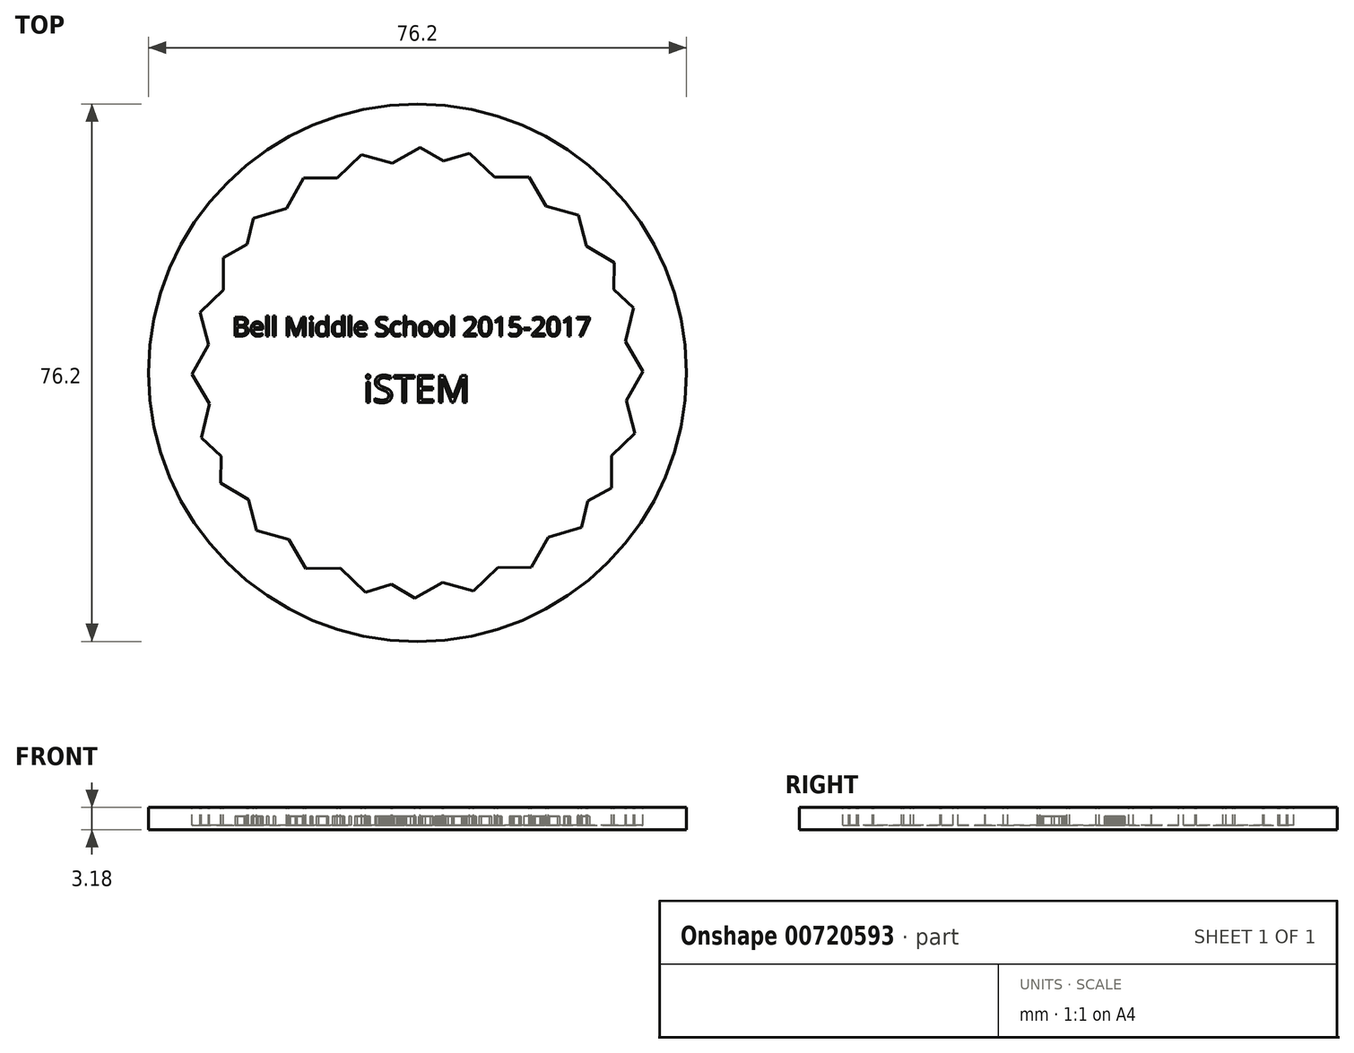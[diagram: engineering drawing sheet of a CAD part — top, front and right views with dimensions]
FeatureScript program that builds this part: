
annotation { "Feature Type Name" : "Feature", "Feature Type Description" : "" }
export const myFeature = defineFeature(function(context is Context, id is Id, definition is map)
    precondition{}
    {
        {
            var Q0;
            Q0=qCreatedBy(makeId("Top.planeOp"),FACE);
            var sketch = newSketch(context, id + "F0", { "sketchPlane" : qUnion([Q0])});
            skCircle(sketch, "E0", {"center": v(0, 0) * mm, "radius": 38.1 * mm});
            skSolve(sketch);
        }
        {
            var Q0;
            Q0=makeQuery(id+"F0.imprint","IMPRINT",FACE,{"disambiguationData":[TD([[makeQuery(id+"F0.imprint","IMPRINT",EDGE,{"derivedFrom":sQuery(id+"F0.wireOp",EDGE,"E0")}),1.0]])]});
            extrude(context, id + "F1", {"entities" : qUnion([Q0]), "depth" : 3.17 * mm, "offsetDistance" : 25.4 * mm});
        }
        {
            var Q0;
            Q0=makeQuery(id+"F1.opExtrude","CAP_FACE",FACE,{"disambiguationData":[OSD([sQuery(id+"F0.wireOp",EDGE,"E0")])],"isStart":false});
            var sketch = newSketch(context, id + "F2", { "sketchPlane" : qUnion([Q0])});
            skCircle(sketch, "E1", {"center": v(0, 0) * mm, "radius": 34.93 * mm});
            skCircle(sketch, "E2.cCircle", {"center": v(0, 0) * mm, "radius": 27.67 * mm, "construction": true});
            skLineSegment(sketch, "E2.0", {"start": v(15.83, 27.75) * mm, "end": v(31.95, 0.17) * mm});
            skLineSegment(sketch, "E2.1", {"start": v(31.95, 0.17) * mm, "end": v(16.12, -27.58) * mm});
            skLineSegment(sketch, "E2.2", {"start": v(16.12, -27.58) * mm, "end": v(-15.83, -27.75) * mm});
            skLineSegment(sketch, "E2.3", {"start": v(-15.83, -27.75) * mm, "end": v(-31.95, -0.17) * mm});
            skLineSegment(sketch, "E2.4", {"start": v(-31.95, -0.17) * mm, "end": v(-16.12, 27.58) * mm});
            skLineSegment(sketch, "E2.5", {"start": v(-16.12, 27.58) * mm, "end": v(15.83, 27.75) * mm});
            skPoint(sketch, "E2.0.midPoint", {"position": v(23.89, 13.96) * mm});
            skLineSegment(sketch, "E3.0", {"start": v(0.4, 31.95) * mm, "end": v(27.87, 15.63) * mm});
            skLineSegment(sketch, "E3.1", {"start": v(27.87, 15.63) * mm, "end": v(27.47, -16.32) * mm});
            skLineSegment(sketch, "E3.2", {"start": v(27.47, -16.32) * mm, "end": v(-0.4, -31.95) * mm});
            skLineSegment(sketch, "E3.3", {"start": v(-0.4, -31.95) * mm, "end": v(-27.87, -15.63) * mm});
            skLineSegment(sketch, "E3.4", {"start": v(-27.87, -15.63) * mm, "end": v(-27.47, 16.32) * mm});
            skLineSegment(sketch, "E3.5", {"start": v(-27.47, 16.32) * mm, "end": v(0.4, 31.95) * mm});
            skPoint(sketch, "E3.0.midPoint", {"position": v(14.13, 23.79) * mm});
            skLineSegment(sketch, "E4.0", {"start": v(22.82, 22.36) * mm, "end": v(30.78, -8.58) * mm});
            skLineSegment(sketch, "E4.1", {"start": v(30.78, -8.58) * mm, "end": v(7.96, -30.94) * mm});
            skLineSegment(sketch, "E4.2", {"start": v(7.96, -30.94) * mm, "end": v(-22.82, -22.36) * mm});
            skLineSegment(sketch, "E4.3", {"start": v(-22.82, -22.36) * mm, "end": v(-30.78, 8.58) * mm});
            skLineSegment(sketch, "E4.4", {"start": v(-30.78, 8.58) * mm, "end": v(-7.96, 30.94) * mm});
            skLineSegment(sketch, "E4.5", {"start": v(-7.96, 30.94) * mm, "end": v(22.82, 22.36) * mm});
            skPoint(sketch, "E4.0.midPoint", {"position": v(26.8, 6.9) * mm});
            skLineSegment(sketch, "E5.0", {"start": v(-23.26, 21.9) * mm, "end": v(7.34, 31.1) * mm});
            skLineSegment(sketch, "E5.1", {"start": v(7.34, 31.1) * mm, "end": v(30.6, 9.19) * mm});
            skLineSegment(sketch, "E5.2", {"start": v(30.6, 9.19) * mm, "end": v(23.26, -21.9) * mm});
            skLineSegment(sketch, "E5.3", {"start": v(23.26, -21.9) * mm, "end": v(-7.34, -31.1) * mm});
            skLineSegment(sketch, "E5.4", {"start": v(-7.34, -31.1) * mm, "end": v(-30.6, -9.19) * mm});
            skLineSegment(sketch, "E5.5", {"start": v(-30.6, -9.19) * mm, "end": v(-23.26, 21.9) * mm});
            skPoint(sketch, "E5.0.midPoint", {"position": v(-7.96, 26.5) * mm});
            skSolve(sketch);
        }
        {
            var Q0;
            {var subQ0=sQuery(id+"F2.wireOp",EDGE,"E4.2");var subQ1=sQuery(id+"F2.wireOp",EDGE,"E2.3");var subQ2=makeQuery(id+"F2.imprint","INTERSECT",VERTEX,{"derivedFrom":[subQ1,subQ0]});Q0=makeQuery(id+"F2.imprint","IMPRINT",FACE,{"disambiguationData":[TD([[makeQuery(id+"F2.imprint","IMPRINT",EDGE,{"disambiguationData":[TD([[subQ2,-1.0]])],"derivedFrom":subQ1}),-1.0]])]});}
            var Q1;
            {var subQ0=sQuery(id+"F2.wireOp",EDGE,"E2.3");var subQ1=sQuery(id+"F2.wireOp",EDGE,"E2.2");var subQ2=makeQuery(id+"F2.imprint","INTERSECT",VERTEX,{"derivedFrom":[subQ1,subQ0]});Q1=makeQuery(id+"F2.imprint","IMPRINT",FACE,{"disambiguationData":[TD([[makeQuery(id+"F2.imprint","IMPRINT",EDGE,{"disambiguationData":[TD([[subQ2,1.0]])],"derivedFrom":subQ1}),-1.0]])]});}
            var Q2;
            {var subQ0=sQuery(id+"F2.wireOp",EDGE,"E4.2");var subQ1=sQuery(id+"F2.wireOp",EDGE,"E2.2");var subQ2=makeQuery(id+"F2.imprint","INTERSECT",VERTEX,{"derivedFrom":[subQ1,subQ0]});Q2=makeQuery(id+"F2.imprint","IMPRINT",FACE,{"disambiguationData":[TD([[makeQuery(id+"F2.imprint","IMPRINT",EDGE,{"disambiguationData":[TD([[subQ2,-1.0]])],"derivedFrom":subQ1}),-1.0]])]});}
            var Q3;
            {var subQ0=sQuery(id+"F2.wireOp",EDGE,"E4.2");var subQ1=sQuery(id+"F2.wireOp",EDGE,"E2.2");var subQ2=makeQuery(id+"F2.imprint","INTERSECT",VERTEX,{"derivedFrom":[subQ1,subQ0]});Q3=makeQuery(id+"F2.imprint","IMPRINT",FACE,{"disambiguationData":[TD([[makeQuery(id+"F2.imprint","IMPRINT",EDGE,{"disambiguationData":[TD([[subQ2,-1.0]])],"derivedFrom":subQ1}),1.0]])]});}
            var Q4;
            {var subQ0=sQuery(id+"F2.wireOp",EDGE,"E3.2");var subQ1=sQuery(id+"F2.wireOp",EDGE,"E2.2");var subQ2=makeQuery(id+"F2.imprint","INTERSECT",VERTEX,{"derivedFrom":[subQ1,subQ0]});Q4=makeQuery(id+"F2.imprint","IMPRINT",FACE,{"disambiguationData":[TD([[makeQuery(id+"F2.imprint","IMPRINT",EDGE,{"disambiguationData":[TD([[subQ2,-1.0]])],"derivedFrom":subQ1}),1.0]])]});}
            var Q5;
            {var subQ0=sQuery(id+"F2.wireOp",EDGE,"E4.1");var subQ1=sQuery(id+"F2.wireOp",EDGE,"E2.2");var subQ2=makeQuery(id+"F2.imprint","INTERSECT",VERTEX,{"derivedFrom":[subQ1,subQ0]});Q5=makeQuery(id+"F2.imprint","IMPRINT",FACE,{"disambiguationData":[TD([[makeQuery(id+"F2.imprint","IMPRINT",EDGE,{"disambiguationData":[TD([[subQ2,-1.0]])],"derivedFrom":subQ1}),1.0]])]});}
            var Q6;
            {var subQ0=sQuery(id+"F2.wireOp",EDGE,"E4.1");var subQ1=sQuery(id+"F2.wireOp",EDGE,"E2.2");var subQ2=makeQuery(id+"F2.imprint","INTERSECT",VERTEX,{"derivedFrom":[subQ1,subQ0]});Q6=makeQuery(id+"F2.imprint","IMPRINT",FACE,{"disambiguationData":[TD([[makeQuery(id+"F2.imprint","IMPRINT",EDGE,{"disambiguationData":[TD([[subQ2,-1.0]])],"derivedFrom":subQ1}),-1.0]])]});}
            var Q7;
            {var subQ0=sQuery(id+"F2.wireOp",EDGE,"E2.2");var subQ1=sQuery(id+"F2.wireOp",EDGE,"E2.1");var subQ2=makeQuery(id+"F2.imprint","INTERSECT",VERTEX,{"derivedFrom":[subQ1,subQ0]});Q7=makeQuery(id+"F2.imprint","IMPRINT",FACE,{"disambiguationData":[TD([[makeQuery(id+"F2.imprint","IMPRINT",EDGE,{"disambiguationData":[TD([[subQ2,1.0]])],"derivedFrom":subQ1}),-1.0]])]});}
            var Q8;
            {var subQ15=sQuery(id+"F2.wireOp",EDGE,"E3.0");var subQ16=sQuery(id+"F2.wireOp",EDGE,"E2.0");var subQ17=makeQuery(id+"F2.imprint","INTERSECT",VERTEX,{"derivedFrom":[subQ16,subQ15]});Q8=makeQuery(id+"F2.imprint","IMPRINT",FACE,{"disambiguationData":[TD([[makeQuery(id+"F2.imprint","IMPRINT",EDGE,{"disambiguationData":[TD([[subQ17,-1.0]])],"derivedFrom":subQ16}),-1.0]])]});}
            var Q9;
            {var subQ0=sQuery(id+"F2.wireOp",EDGE,"E4.1");var subQ1=sQuery(id+"F2.wireOp",EDGE,"E2.1");var subQ2=makeQuery(id+"F2.imprint","INTERSECT",VERTEX,{"derivedFrom":[subQ1,subQ0]});Q9=makeQuery(id+"F2.imprint","IMPRINT",FACE,{"disambiguationData":[TD([[makeQuery(id+"F2.imprint","IMPRINT",EDGE,{"disambiguationData":[TD([[subQ2,-1.0]])],"derivedFrom":subQ1}),-1.0]])]});}
            var Q10;
            {var subQ0=sQuery(id+"F2.wireOp",EDGE,"E4.1");var subQ1=sQuery(id+"F2.wireOp",EDGE,"E2.1");var subQ2=makeQuery(id+"F2.imprint","INTERSECT",VERTEX,{"derivedFrom":[subQ1,subQ0]});Q10=makeQuery(id+"F2.imprint","IMPRINT",FACE,{"disambiguationData":[TD([[makeQuery(id+"F2.imprint","IMPRINT",EDGE,{"disambiguationData":[TD([[subQ2,-1.0]])],"derivedFrom":subQ1}),1.0]])]});}
            var Q11;
            {var subQ0=sQuery(id+"F2.wireOp",EDGE,"E3.1");var subQ1=sQuery(id+"F2.wireOp",EDGE,"E2.1");var subQ2=makeQuery(id+"F2.imprint","INTERSECT",VERTEX,{"derivedFrom":[subQ1,subQ0]});Q11=makeQuery(id+"F2.imprint","IMPRINT",FACE,{"disambiguationData":[TD([[makeQuery(id+"F2.imprint","IMPRINT",EDGE,{"disambiguationData":[TD([[subQ2,-1.0]])],"derivedFrom":subQ1}),1.0]])]});}
            var Q12;
            {var subQ0=sQuery(id+"F2.wireOp",EDGE,"E4.0");var subQ1=sQuery(id+"F2.wireOp",EDGE,"E2.1");var subQ2=makeQuery(id+"F2.imprint","INTERSECT",VERTEX,{"derivedFrom":[subQ1,subQ0]});Q12=makeQuery(id+"F2.imprint","IMPRINT",FACE,{"disambiguationData":[TD([[makeQuery(id+"F2.imprint","IMPRINT",EDGE,{"disambiguationData":[TD([[subQ2,-1.0]])],"derivedFrom":subQ1}),1.0]])]});}
            var Q13;
            {var subQ0=sQuery(id+"F2.wireOp",EDGE,"E4.0");var subQ1=sQuery(id+"F2.wireOp",EDGE,"E2.1");var subQ2=makeQuery(id+"F2.imprint","INTERSECT",VERTEX,{"derivedFrom":[subQ1,subQ0]});Q13=makeQuery(id+"F2.imprint","IMPRINT",FACE,{"disambiguationData":[TD([[makeQuery(id+"F2.imprint","IMPRINT",EDGE,{"disambiguationData":[TD([[subQ2,-1.0]])],"derivedFrom":subQ1}),-1.0]])]});}
            var Q14;
            {var subQ0=sQuery(id+"F2.wireOp",EDGE,"E2.1");var subQ1=sQuery(id+"F2.wireOp",EDGE,"E2.0");var subQ2=makeQuery(id+"F2.imprint","INTERSECT",VERTEX,{"derivedFrom":[subQ1,subQ0]});Q14=makeQuery(id+"F2.imprint","IMPRINT",FACE,{"disambiguationData":[TD([[makeQuery(id+"F2.imprint","IMPRINT",EDGE,{"disambiguationData":[TD([[subQ2,1.0]])],"derivedFrom":subQ1}),-1.0]])]});}
            var Q15;
            {var subQ0=sQuery(id+"F2.wireOp",EDGE,"E4.0");var subQ1=sQuery(id+"F2.wireOp",EDGE,"E2.0");var subQ2=makeQuery(id+"F2.imprint","INTERSECT",VERTEX,{"derivedFrom":[subQ1,subQ0]});Q15=makeQuery(id+"F2.imprint","IMPRINT",FACE,{"disambiguationData":[TD([[makeQuery(id+"F2.imprint","IMPRINT",EDGE,{"disambiguationData":[TD([[subQ2,-1.0]])],"derivedFrom":subQ1}),-1.0]])]});}
            var Q16;
            {var subQ0=sQuery(id+"F2.wireOp",EDGE,"E4.0");var subQ1=sQuery(id+"F2.wireOp",EDGE,"E2.0");var subQ2=makeQuery(id+"F2.imprint","INTERSECT",VERTEX,{"derivedFrom":[subQ1,subQ0]});Q16=makeQuery(id+"F2.imprint","IMPRINT",FACE,{"disambiguationData":[TD([[makeQuery(id+"F2.imprint","IMPRINT",EDGE,{"disambiguationData":[TD([[subQ2,-1.0]])],"derivedFrom":subQ1}),1.0]])]});}
            var Q17;
            {var subQ0=sQuery(id+"F2.wireOp",EDGE,"E3.0");var subQ1=sQuery(id+"F2.wireOp",EDGE,"E2.0");var subQ2=makeQuery(id+"F2.imprint","INTERSECT",VERTEX,{"derivedFrom":[subQ1,subQ0]});Q17=makeQuery(id+"F2.imprint","IMPRINT",FACE,{"disambiguationData":[TD([[makeQuery(id+"F2.imprint","IMPRINT",EDGE,{"disambiguationData":[TD([[subQ2,-1.0]])],"derivedFrom":subQ1}),1.0]])]});}
            var Q18;
            {var subQ0=sQuery(id+"F2.wireOp",EDGE,"E4.5");var subQ1=sQuery(id+"F2.wireOp",EDGE,"E2.0");var subQ2=makeQuery(id+"F2.imprint","INTERSECT",VERTEX,{"derivedFrom":[subQ1,subQ0]});Q18=makeQuery(id+"F2.imprint","IMPRINT",FACE,{"disambiguationData":[TD([[makeQuery(id+"F2.imprint","IMPRINT",EDGE,{"disambiguationData":[TD([[subQ2,-1.0]])],"derivedFrom":subQ1}),1.0]])]});}
            var Q19;
            {var subQ0=sQuery(id+"F2.wireOp",EDGE,"E4.5");var subQ1=sQuery(id+"F2.wireOp",EDGE,"E2.0");var subQ2=makeQuery(id+"F2.imprint","INTERSECT",VERTEX,{"derivedFrom":[subQ1,subQ0]});Q19=makeQuery(id+"F2.imprint","IMPRINT",FACE,{"disambiguationData":[TD([[makeQuery(id+"F2.imprint","IMPRINT",EDGE,{"disambiguationData":[TD([[subQ2,-1.0]])],"derivedFrom":subQ1}),-1.0]])]});}
            var Q20;
            {var subQ0=sQuery(id+"F2.wireOp",EDGE,"E2.5");var subQ1=sQuery(id+"F2.wireOp",EDGE,"E2.0");var subQ2=makeQuery(id+"F2.imprint","INTERSECT",VERTEX,{"derivedFrom":[subQ1,subQ0]});Q20=makeQuery(id+"F2.imprint","IMPRINT",FACE,{"disambiguationData":[TD([[makeQuery(id+"F2.imprint","IMPRINT",EDGE,{"disambiguationData":[TD([[subQ2,-1.0]])],"derivedFrom":subQ1}),-1.0]])]});}
            var Q21;
            {var subQ0=sQuery(id+"F2.wireOp",EDGE,"E4.5");var subQ1=sQuery(id+"F2.wireOp",EDGE,"E2.5");var subQ2=makeQuery(id+"F2.imprint","INTERSECT",VERTEX,{"derivedFrom":[subQ1,subQ0]});Q21=makeQuery(id+"F2.imprint","IMPRINT",FACE,{"disambiguationData":[TD([[makeQuery(id+"F2.imprint","IMPRINT",EDGE,{"disambiguationData":[TD([[subQ2,-1.0]])],"derivedFrom":subQ1}),1.0]])]});}
            var Q22;
            {var subQ0=sQuery(id+"F2.wireOp",EDGE,"E3.5");var subQ1=sQuery(id+"F2.wireOp",EDGE,"E2.5");var subQ2=makeQuery(id+"F2.imprint","INTERSECT",VERTEX,{"derivedFrom":[subQ1,subQ0]});Q22=makeQuery(id+"F2.imprint","IMPRINT",FACE,{"disambiguationData":[TD([[makeQuery(id+"F2.imprint","IMPRINT",EDGE,{"disambiguationData":[TD([[subQ2,-1.0]])],"derivedFrom":subQ1}),1.0]])]});}
            var Q23;
            {var subQ0=sQuery(id+"F2.wireOp",EDGE,"E4.5");var subQ1=sQuery(id+"F2.wireOp",EDGE,"E2.5");var subQ2=makeQuery(id+"F2.imprint","INTERSECT",VERTEX,{"derivedFrom":[subQ1,subQ0]});Q23=makeQuery(id+"F2.imprint","IMPRINT",FACE,{"disambiguationData":[TD([[makeQuery(id+"F2.imprint","IMPRINT",EDGE,{"disambiguationData":[TD([[subQ2,-1.0]])],"derivedFrom":subQ1}),-1.0]])]});}
            var Q24;
            {var subQ0=sQuery(id+"F2.wireOp",EDGE,"E4.4");var subQ1=sQuery(id+"F2.wireOp",EDGE,"E2.5");var subQ2=makeQuery(id+"F2.imprint","INTERSECT",VERTEX,{"derivedFrom":[subQ1,subQ0]});Q24=makeQuery(id+"F2.imprint","IMPRINT",FACE,{"disambiguationData":[TD([[makeQuery(id+"F2.imprint","IMPRINT",EDGE,{"disambiguationData":[TD([[subQ2,-1.0]])],"derivedFrom":subQ1}),-1.0]])]});}
            var Q25;
            {var subQ0=sQuery(id+"F2.wireOp",EDGE,"E4.4");var subQ1=sQuery(id+"F2.wireOp",EDGE,"E2.5");var subQ2=makeQuery(id+"F2.imprint","INTERSECT",VERTEX,{"derivedFrom":[subQ1,subQ0]});Q25=makeQuery(id+"F2.imprint","IMPRINT",FACE,{"disambiguationData":[TD([[makeQuery(id+"F2.imprint","IMPRINT",EDGE,{"disambiguationData":[TD([[subQ2,-1.0]])],"derivedFrom":subQ1}),1.0]])]});}
            var Q26;
            {var subQ0=sQuery(id+"F2.wireOp",EDGE,"E2.5");var subQ1=sQuery(id+"F2.wireOp",EDGE,"E2.4");var subQ2=makeQuery(id+"F2.imprint","INTERSECT",VERTEX,{"derivedFrom":[subQ1,subQ0]});Q26=makeQuery(id+"F2.imprint","IMPRINT",FACE,{"disambiguationData":[TD([[makeQuery(id+"F2.imprint","IMPRINT",EDGE,{"disambiguationData":[TD([[subQ2,1.0]])],"derivedFrom":subQ1}),-1.0]])]});}
            var Q27;
            {var subQ0=sQuery(id+"F2.wireOp",EDGE,"E4.4");var subQ1=sQuery(id+"F2.wireOp",EDGE,"E2.4");var subQ2=makeQuery(id+"F2.imprint","INTERSECT",VERTEX,{"derivedFrom":[subQ1,subQ0]});Q27=makeQuery(id+"F2.imprint","IMPRINT",FACE,{"disambiguationData":[TD([[makeQuery(id+"F2.imprint","IMPRINT",EDGE,{"disambiguationData":[TD([[subQ2,-1.0]])],"derivedFrom":subQ1}),-1.0]])]});}
            var Q28;
            {var subQ0=sQuery(id+"F2.wireOp",EDGE,"E4.4");var subQ1=sQuery(id+"F2.wireOp",EDGE,"E2.4");var subQ2=makeQuery(id+"F2.imprint","INTERSECT",VERTEX,{"derivedFrom":[subQ1,subQ0]});Q28=makeQuery(id+"F2.imprint","IMPRINT",FACE,{"disambiguationData":[TD([[makeQuery(id+"F2.imprint","IMPRINT",EDGE,{"disambiguationData":[TD([[subQ2,-1.0]])],"derivedFrom":subQ1}),1.0]])]});}
            var Q29;
            {var subQ0=sQuery(id+"F2.wireOp",EDGE,"E3.4");var subQ1=sQuery(id+"F2.wireOp",EDGE,"E2.4");var subQ2=makeQuery(id+"F2.imprint","INTERSECT",VERTEX,{"derivedFrom":[subQ1,subQ0]});Q29=makeQuery(id+"F2.imprint","IMPRINT",FACE,{"disambiguationData":[TD([[makeQuery(id+"F2.imprint","IMPRINT",EDGE,{"disambiguationData":[TD([[subQ2,-1.0]])],"derivedFrom":subQ1}),1.0]])]});}
            var Q30;
            {var subQ0=sQuery(id+"F2.wireOp",EDGE,"E4.3");var subQ1=sQuery(id+"F2.wireOp",EDGE,"E2.4");var subQ2=makeQuery(id+"F2.imprint","INTERSECT",VERTEX,{"derivedFrom":[subQ1,subQ0]});Q30=makeQuery(id+"F2.imprint","IMPRINT",FACE,{"disambiguationData":[TD([[makeQuery(id+"F2.imprint","IMPRINT",EDGE,{"disambiguationData":[TD([[subQ2,-1.0]])],"derivedFrom":subQ1}),1.0]])]});}
            var Q31;
            {var subQ0=sQuery(id+"F2.wireOp",EDGE,"E4.3");var subQ1=sQuery(id+"F2.wireOp",EDGE,"E2.4");var subQ2=makeQuery(id+"F2.imprint","INTERSECT",VERTEX,{"derivedFrom":[subQ1,subQ0]});Q31=makeQuery(id+"F2.imprint","IMPRINT",FACE,{"disambiguationData":[TD([[makeQuery(id+"F2.imprint","IMPRINT",EDGE,{"disambiguationData":[TD([[subQ2,-1.0]])],"derivedFrom":subQ1}),-1.0]])]});}
            var Q32;
            {var subQ0=sQuery(id+"F2.wireOp",EDGE,"E2.4");var subQ1=sQuery(id+"F2.wireOp",EDGE,"E2.3");var subQ2=makeQuery(id+"F2.imprint","INTERSECT",VERTEX,{"derivedFrom":[subQ1,subQ0]});Q32=makeQuery(id+"F2.imprint","IMPRINT",FACE,{"disambiguationData":[TD([[makeQuery(id+"F2.imprint","IMPRINT",EDGE,{"disambiguationData":[TD([[subQ2,1.0]])],"derivedFrom":subQ1}),-1.0]])]});}
            var Q33;
            {var subQ0=sQuery(id+"F2.wireOp",EDGE,"E4.3");var subQ1=sQuery(id+"F2.wireOp",EDGE,"E2.3");var subQ2=makeQuery(id+"F2.imprint","INTERSECT",VERTEX,{"derivedFrom":[subQ1,subQ0]});Q33=makeQuery(id+"F2.imprint","IMPRINT",FACE,{"disambiguationData":[TD([[makeQuery(id+"F2.imprint","IMPRINT",EDGE,{"disambiguationData":[TD([[subQ2,-1.0]])],"derivedFrom":subQ1}),-1.0]])]});}
            var Q34;
            {var subQ0=sQuery(id+"F2.wireOp",EDGE,"E3.3");var subQ1=sQuery(id+"F2.wireOp",EDGE,"E2.3");var subQ2=makeQuery(id+"F2.imprint","INTERSECT",VERTEX,{"derivedFrom":[subQ1,subQ0]});Q34=makeQuery(id+"F2.imprint","IMPRINT",FACE,{"disambiguationData":[TD([[makeQuery(id+"F2.imprint","IMPRINT",EDGE,{"disambiguationData":[TD([[subQ2,-1.0]])],"derivedFrom":subQ1}),1.0]])]});}
            var Q35;
            {var subQ0=sQuery(id+"F2.wireOp",EDGE,"E4.3");var subQ1=sQuery(id+"F2.wireOp",EDGE,"E2.3");var subQ2=makeQuery(id+"F2.imprint","INTERSECT",VERTEX,{"derivedFrom":[subQ1,subQ0]});Q35=makeQuery(id+"F2.imprint","IMPRINT",FACE,{"disambiguationData":[TD([[makeQuery(id+"F2.imprint","IMPRINT",EDGE,{"disambiguationData":[TD([[subQ2,-1.0]])],"derivedFrom":subQ1}),1.0]])]});}
            var Q36;
            {var subQ0=sQuery(id+"F2.wireOp",EDGE,"E3.4");var subQ1=sQuery(id+"F2.wireOp",EDGE,"E3.3");var subQ2=makeQuery(id+"F2.imprint","INTERSECT",VERTEX,{"derivedFrom":[subQ1,subQ0]});Q36=makeQuery(id+"F2.imprint","IMPRINT",FACE,{"disambiguationData":[TD([[makeQuery(id+"F2.imprint","IMPRINT",EDGE,{"disambiguationData":[TD([[subQ2,1.0]])],"derivedFrom":subQ1}),-1.0]])]});}
            var Q37;
            {var subQ0=sQuery(id+"F2.wireOp",EDGE,"E3.4");var subQ1=sQuery(id+"F2.wireOp",EDGE,"E2.3");var subQ2=makeQuery(id+"F2.imprint","INTERSECT",VERTEX,{"derivedFrom":[subQ1,subQ0]});Q37=makeQuery(id+"F2.imprint","IMPRINT",FACE,{"disambiguationData":[TD([[makeQuery(id+"F2.imprint","IMPRINT",EDGE,{"disambiguationData":[TD([[subQ2,-1.0]])],"derivedFrom":subQ1}),1.0]])]});}
            var Q38;
            {var subQ0=sQuery(id+"F2.wireOp",EDGE,"E3.4");var subQ1=sQuery(id+"F2.wireOp",EDGE,"E2.3");var subQ2=makeQuery(id+"F2.imprint","INTERSECT",VERTEX,{"derivedFrom":[subQ1,subQ0]});Q38=makeQuery(id+"F2.imprint","IMPRINT",FACE,{"disambiguationData":[TD([[makeQuery(id+"F2.imprint","IMPRINT",EDGE,{"disambiguationData":[TD([[subQ2,-1.0]])],"derivedFrom":subQ1}),-1.0]])]});}
            var Q39;
            {var subQ0=sQuery(id+"F2.wireOp",EDGE,"E4.3");var subQ1=sQuery(id+"F2.wireOp",EDGE,"E3.4");var subQ2=makeQuery(id+"F2.imprint","INTERSECT",VERTEX,{"derivedFrom":[subQ1,subQ0]});Q39=makeQuery(id+"F2.imprint","IMPRINT",FACE,{"disambiguationData":[TD([[makeQuery(id+"F2.imprint","IMPRINT",EDGE,{"disambiguationData":[TD([[subQ2,-1.0]])],"derivedFrom":subQ1}),1.0]])]});}
            var Q40;
            {var subQ0=sQuery(id+"F2.wireOp",EDGE,"E3.4");var subQ1=sQuery(id+"F2.wireOp",EDGE,"E2.4");var subQ2=makeQuery(id+"F2.imprint","INTERSECT",VERTEX,{"derivedFrom":[subQ1,subQ0]});Q40=makeQuery(id+"F2.imprint","IMPRINT",FACE,{"disambiguationData":[TD([[makeQuery(id+"F2.imprint","IMPRINT",EDGE,{"disambiguationData":[TD([[subQ2,-1.0]])],"derivedFrom":subQ1}),-1.0]])]});}
            var Q41;
            {var subQ0=sQuery(id+"F2.wireOp",EDGE,"E5.5");var subQ1=sQuery(id+"F2.wireOp",EDGE,"E2.4");var subQ2=makeQuery(id+"F2.imprint","INTERSECT",VERTEX,{"derivedFrom":[subQ1,subQ0]});Q41=makeQuery(id+"F2.imprint","IMPRINT",FACE,{"disambiguationData":[TD([[makeQuery(id+"F2.imprint","IMPRINT",EDGE,{"disambiguationData":[TD([[subQ2,-1.0]])],"derivedFrom":subQ1}),1.0]])]});}
            var Q42;
            {var subQ0=sQuery(id+"F2.wireOp",EDGE,"E3.5");var subQ1=sQuery(id+"F2.wireOp",EDGE,"E3.4");var subQ2=makeQuery(id+"F2.imprint","INTERSECT",VERTEX,{"derivedFrom":[subQ1,subQ0]});Q42=makeQuery(id+"F2.imprint","IMPRINT",FACE,{"disambiguationData":[TD([[makeQuery(id+"F2.imprint","IMPRINT",EDGE,{"disambiguationData":[TD([[subQ2,1.0]])],"derivedFrom":subQ1}),-1.0]])]});}
            var Q43;
            {var subQ0=sQuery(id+"F2.wireOp",EDGE,"E3.5");var subQ1=sQuery(id+"F2.wireOp",EDGE,"E2.4");var subQ2=makeQuery(id+"F2.imprint","INTERSECT",VERTEX,{"derivedFrom":[subQ1,subQ0]});Q43=makeQuery(id+"F2.imprint","IMPRINT",FACE,{"disambiguationData":[TD([[makeQuery(id+"F2.imprint","IMPRINT",EDGE,{"disambiguationData":[TD([[subQ2,-1.0]])],"derivedFrom":subQ1}),1.0]])]});}
            var Q44;
            {var subQ0=sQuery(id+"F2.wireOp",EDGE,"E3.0");var subQ1=sQuery(id+"F2.wireOp",EDGE,"E2.5");var subQ2=makeQuery(id+"F2.imprint","INTERSECT",VERTEX,{"derivedFrom":[subQ1,subQ0]});Q44=makeQuery(id+"F2.imprint","IMPRINT",FACE,{"disambiguationData":[TD([[makeQuery(id+"F2.imprint","IMPRINT",EDGE,{"disambiguationData":[TD([[subQ2,-1.0]])],"derivedFrom":subQ1}),1.0]])]});}
            var Q45;
            {var subQ0=sQuery(id+"F2.wireOp",EDGE,"E3.5");var subQ1=sQuery(id+"F2.wireOp",EDGE,"E3.0");var subQ2=makeQuery(id+"F2.imprint","INTERSECT",VERTEX,{"derivedFrom":[subQ1,subQ0]});Q45=makeQuery(id+"F2.imprint","IMPRINT",FACE,{"disambiguationData":[TD([[makeQuery(id+"F2.imprint","IMPRINT",EDGE,{"disambiguationData":[TD([[subQ2,-1.0]])],"derivedFrom":subQ1}),-1.0]])]});}
            var Q46;
            {var subQ0=sQuery(id+"F2.wireOp",EDGE,"E5.0");var subQ1=sQuery(id+"F2.wireOp",EDGE,"E2.5");var subQ2=makeQuery(id+"F2.imprint","INTERSECT",VERTEX,{"derivedFrom":[subQ1,subQ0]});Q46=makeQuery(id+"F2.imprint","IMPRINT",FACE,{"disambiguationData":[TD([[makeQuery(id+"F2.imprint","IMPRINT",EDGE,{"disambiguationData":[TD([[subQ2,-1.0]])],"derivedFrom":subQ1}),1.0]])]});}
            var Q47;
            {var subQ0=sQuery(id+"F2.wireOp",EDGE,"E3.5");var subQ1=sQuery(id+"F2.wireOp",EDGE,"E2.5");var subQ2=makeQuery(id+"F2.imprint","INTERSECT",VERTEX,{"derivedFrom":[subQ1,subQ0]});Q47=makeQuery(id+"F2.imprint","IMPRINT",FACE,{"disambiguationData":[TD([[makeQuery(id+"F2.imprint","IMPRINT",EDGE,{"disambiguationData":[TD([[subQ2,-1.0]])],"derivedFrom":subQ1}),-1.0]])]});}
            var Q48;
            {var subQ0=sQuery(id+"F2.wireOp",EDGE,"E3.5");var subQ1=sQuery(id+"F2.wireOp",EDGE,"E2.4");var subQ2=makeQuery(id+"F2.imprint","INTERSECT",VERTEX,{"derivedFrom":[subQ1,subQ0]});Q48=makeQuery(id+"F2.imprint","IMPRINT",FACE,{"disambiguationData":[TD([[makeQuery(id+"F2.imprint","IMPRINT",EDGE,{"disambiguationData":[TD([[subQ2,-1.0]])],"derivedFrom":subQ1}),-1.0]])]});}
            var Q49;
            {var subQ0=sQuery(id+"F2.wireOp",EDGE,"E3.1");var subQ1=sQuery(id+"F2.wireOp",EDGE,"E2.0");var subQ2=makeQuery(id+"F2.imprint","INTERSECT",VERTEX,{"derivedFrom":[subQ1,subQ0]});Q49=makeQuery(id+"F2.imprint","IMPRINT",FACE,{"disambiguationData":[TD([[makeQuery(id+"F2.imprint","IMPRINT",EDGE,{"disambiguationData":[TD([[subQ2,-1.0]])],"derivedFrom":subQ1}),1.0]])]});}
            var Q50;
            {var subQ0=sQuery(id+"F2.wireOp",EDGE,"E3.1");var subQ1=sQuery(id+"F2.wireOp",EDGE,"E3.0");var subQ2=makeQuery(id+"F2.imprint","INTERSECT",VERTEX,{"derivedFrom":[subQ1,subQ0]});Q50=makeQuery(id+"F2.imprint","IMPRINT",FACE,{"disambiguationData":[TD([[makeQuery(id+"F2.imprint","IMPRINT",EDGE,{"disambiguationData":[TD([[subQ2,1.0]])],"derivedFrom":subQ1}),-1.0]])]});}
            var Q51;
            {var subQ0=sQuery(id+"F2.wireOp",EDGE,"E3.1");var subQ1=sQuery(id+"F2.wireOp",EDGE,"E2.0");var subQ2=makeQuery(id+"F2.imprint","INTERSECT",VERTEX,{"derivedFrom":[subQ1,subQ0]});Q51=makeQuery(id+"F2.imprint","IMPRINT",FACE,{"disambiguationData":[TD([[makeQuery(id+"F2.imprint","IMPRINT",EDGE,{"disambiguationData":[TD([[subQ2,-1.0]])],"derivedFrom":subQ1}),-1.0]])]});}
            var Q52;
            {var subQ0=sQuery(id+"F2.wireOp",EDGE,"E3.2");var subQ1=sQuery(id+"F2.wireOp",EDGE,"E3.1");var subQ2=makeQuery(id+"F2.imprint","INTERSECT",VERTEX,{"derivedFrom":[subQ1,subQ0]});Q52=makeQuery(id+"F2.imprint","IMPRINT",FACE,{"disambiguationData":[TD([[makeQuery(id+"F2.imprint","IMPRINT",EDGE,{"disambiguationData":[TD([[subQ2,1.0]])],"derivedFrom":subQ1}),-1.0]])]});}
            var Q53;
            {var subQ0=sQuery(id+"F2.wireOp",EDGE,"E3.2");var subQ1=sQuery(id+"F2.wireOp",EDGE,"E2.1");var subQ2=makeQuery(id+"F2.imprint","INTERSECT",VERTEX,{"derivedFrom":[subQ1,subQ0]});Q53=makeQuery(id+"F2.imprint","IMPRINT",FACE,{"disambiguationData":[TD([[makeQuery(id+"F2.imprint","IMPRINT",EDGE,{"disambiguationData":[TD([[subQ2,-1.0]])],"derivedFrom":subQ1}),1.0]])]});}
            var Q54;
            {var subQ0=sQuery(id+"F2.wireOp",EDGE,"E3.2");var subQ1=sQuery(id+"F2.wireOp",EDGE,"E2.1");var subQ2=makeQuery(id+"F2.imprint","INTERSECT",VERTEX,{"derivedFrom":[subQ1,subQ0]});Q54=makeQuery(id+"F2.imprint","IMPRINT",FACE,{"disambiguationData":[TD([[makeQuery(id+"F2.imprint","IMPRINT",EDGE,{"disambiguationData":[TD([[subQ2,-1.0]])],"derivedFrom":subQ1}),-1.0]])]});}
            var Q55;
            {var subQ0=sQuery(id+"F2.wireOp",EDGE,"E3.3");var subQ1=sQuery(id+"F2.wireOp",EDGE,"E3.2");var subQ2=makeQuery(id+"F2.imprint","INTERSECT",VERTEX,{"derivedFrom":[subQ1,subQ0]});Q55=makeQuery(id+"F2.imprint","IMPRINT",FACE,{"disambiguationData":[TD([[makeQuery(id+"F2.imprint","IMPRINT",EDGE,{"disambiguationData":[TD([[subQ2,1.0]])],"derivedFrom":subQ1}),-1.0]])]});}
            var Q56;
            {var subQ0=sQuery(id+"F2.wireOp",EDGE,"E3.3");var subQ1=sQuery(id+"F2.wireOp",EDGE,"E2.2");var subQ2=makeQuery(id+"F2.imprint","INTERSECT",VERTEX,{"derivedFrom":[subQ1,subQ0]});Q56=makeQuery(id+"F2.imprint","IMPRINT",FACE,{"disambiguationData":[TD([[makeQuery(id+"F2.imprint","IMPRINT",EDGE,{"disambiguationData":[TD([[subQ2,-1.0]])],"derivedFrom":subQ1}),1.0]])]});}
            var Q57;
            {var subQ0=sQuery(id+"F2.wireOp",EDGE,"E3.3");var subQ1=sQuery(id+"F2.wireOp",EDGE,"E2.2");var subQ2=makeQuery(id+"F2.imprint","INTERSECT",VERTEX,{"derivedFrom":[subQ1,subQ0]});Q57=makeQuery(id+"F2.imprint","IMPRINT",FACE,{"disambiguationData":[TD([[makeQuery(id+"F2.imprint","IMPRINT",EDGE,{"disambiguationData":[TD([[subQ2,-1.0]])],"derivedFrom":subQ1}),-1.0]])]});}
            var Q58;
            {var subQ0=sQuery(id+"F2.wireOp",EDGE,"E3.0");var subQ1=sQuery(id+"F2.wireOp",EDGE,"E2.5");var subQ2=makeQuery(id+"F2.imprint","INTERSECT",VERTEX,{"derivedFrom":[subQ1,subQ0]});Q58=makeQuery(id+"F2.imprint","IMPRINT",FACE,{"disambiguationData":[TD([[makeQuery(id+"F2.imprint","IMPRINT",EDGE,{"disambiguationData":[TD([[subQ2,-1.0]])],"derivedFrom":subQ1}),-1.0]])]});}
            var Q59;
            {var subQ10=sQuery(id+"F2.wireOp",EDGE,"E5.1");var subQ11=sQuery(id+"F2.wireOp",EDGE,"E2.0");var subQ12=makeQuery(id+"F2.imprint","INTERSECT",VERTEX,{"derivedFrom":[subQ11,subQ10]});Q59=makeQuery(id+"F2.imprint","IMPRINT",FACE,{"disambiguationData":[TD([[makeQuery(id+"F2.imprint","IMPRINT",EDGE,{"disambiguationData":[TD([[subQ12,-1.0]])],"derivedFrom":subQ11}),-1.0]])]});}
            var Q60;
            {var subQ0=sQuery(id+"F2.wireOp",EDGE,"E3.1");var subQ1=sQuery(id+"F2.wireOp",EDGE,"E2.1");var subQ2=makeQuery(id+"F2.imprint","INTERSECT",VERTEX,{"derivedFrom":[subQ1,subQ0]});Q60=makeQuery(id+"F2.imprint","IMPRINT",FACE,{"disambiguationData":[TD([[makeQuery(id+"F2.imprint","IMPRINT",EDGE,{"disambiguationData":[TD([[subQ2,-1.0]])],"derivedFrom":subQ1}),-1.0]])]});}
            var Q61;
            {var subQ0=sQuery(id+"F2.wireOp",EDGE,"E5.2");var subQ1=sQuery(id+"F2.wireOp",EDGE,"E2.1");var subQ2=makeQuery(id+"F2.imprint","INTERSECT",VERTEX,{"derivedFrom":[subQ1,subQ0]});Q61=makeQuery(id+"F2.imprint","IMPRINT",FACE,{"disambiguationData":[TD([[makeQuery(id+"F2.imprint","IMPRINT",EDGE,{"disambiguationData":[TD([[subQ2,-1.0]])],"derivedFrom":subQ1}),1.0]])]});}
            var Q62;
            {var subQ0=sQuery(id+"F2.wireOp",EDGE,"E3.2");var subQ1=sQuery(id+"F2.wireOp",EDGE,"E2.2");var subQ2=makeQuery(id+"F2.imprint","INTERSECT",VERTEX,{"derivedFrom":[subQ1,subQ0]});Q62=makeQuery(id+"F2.imprint","IMPRINT",FACE,{"disambiguationData":[TD([[makeQuery(id+"F2.imprint","IMPRINT",EDGE,{"disambiguationData":[TD([[subQ2,-1.0]])],"derivedFrom":subQ1}),-1.0]])]});}
            var Q63;
            {var subQ0=sQuery(id+"F2.wireOp",EDGE,"E4.1");var subQ1=sQuery(id+"F2.wireOp",EDGE,"E3.2");var subQ2=makeQuery(id+"F2.imprint","INTERSECT",VERTEX,{"derivedFrom":[subQ1,subQ0]});Q63=makeQuery(id+"F2.imprint","IMPRINT",FACE,{"disambiguationData":[TD([[makeQuery(id+"F2.imprint","IMPRINT",EDGE,{"disambiguationData":[TD([[subQ2,-1.0]])],"derivedFrom":subQ1}),1.0]])]});}
            var Q64;
            {var subQ0=sQuery(id+"F2.wireOp",EDGE,"E5.3");var subQ1=sQuery(id+"F2.wireOp",EDGE,"E2.2");var subQ2=makeQuery(id+"F2.imprint","INTERSECT",VERTEX,{"derivedFrom":[subQ1,subQ0]});Q64=makeQuery(id+"F2.imprint","IMPRINT",FACE,{"disambiguationData":[TD([[makeQuery(id+"F2.imprint","IMPRINT",EDGE,{"disambiguationData":[TD([[subQ2,-1.0]])],"derivedFrom":subQ1}),1.0]])]});}
            var Q65;
            {var subQ0=sQuery(id+"F2.wireOp",EDGE,"E4.2");var subQ1=sQuery(id+"F2.wireOp",EDGE,"E3.3");var subQ2=makeQuery(id+"F2.imprint","INTERSECT",VERTEX,{"derivedFrom":[subQ1,subQ0]});Q65=makeQuery(id+"F2.imprint","IMPRINT",FACE,{"disambiguationData":[TD([[makeQuery(id+"F2.imprint","IMPRINT",EDGE,{"disambiguationData":[TD([[subQ2,-1.0]])],"derivedFrom":subQ1}),1.0]])]});}
            var Q66;
            {var subQ0=sQuery(id+"F2.wireOp",EDGE,"E4.2");var subQ1=sQuery(id+"F2.wireOp",EDGE,"E2.3");var subQ2=makeQuery(id+"F2.imprint","INTERSECT",VERTEX,{"derivedFrom":[subQ1,subQ0]});Q66=makeQuery(id+"F2.imprint","IMPRINT",FACE,{"disambiguationData":[TD([[makeQuery(id+"F2.imprint","IMPRINT",EDGE,{"disambiguationData":[TD([[subQ2,-1.0]])],"derivedFrom":subQ1}),1.0]])]});}
            var Q67;
            {var subQ0=sQuery(id+"F2.wireOp",EDGE,"E5.4");var subQ1=sQuery(id+"F2.wireOp",EDGE,"E2.3");var subQ2=makeQuery(id+"F2.imprint","INTERSECT",VERTEX,{"derivedFrom":[subQ1,subQ0]});Q67=makeQuery(id+"F2.imprint","IMPRINT",FACE,{"disambiguationData":[TD([[makeQuery(id+"F2.imprint","IMPRINT",EDGE,{"disambiguationData":[TD([[subQ2,-1.0]])],"derivedFrom":subQ1}),1.0]])]});}
            var Q68;
            {var subQ0=sQuery(id+"F2.wireOp",EDGE,"E3.3");var subQ1=sQuery(id+"F2.wireOp",EDGE,"E2.3");var subQ2=makeQuery(id+"F2.imprint","INTERSECT",VERTEX,{"derivedFrom":[subQ1,subQ0]});Q68=makeQuery(id+"F2.imprint","IMPRINT",FACE,{"disambiguationData":[TD([[makeQuery(id+"F2.imprint","IMPRINT",EDGE,{"disambiguationData":[TD([[subQ2,-1.0]])],"derivedFrom":subQ1}),-1.0]])]});}
            var Q69;
            {var subQ0=sQuery(id+"F2.wireOp",EDGE,"E4.5");var subQ1=sQuery(id+"F2.wireOp",EDGE,"E3.0");var subQ2=makeQuery(id+"F2.imprint","INTERSECT",VERTEX,{"derivedFrom":[subQ1,subQ0]});Q69=makeQuery(id+"F2.imprint","IMPRINT",FACE,{"disambiguationData":[TD([[makeQuery(id+"F2.imprint","IMPRINT",EDGE,{"disambiguationData":[TD([[subQ2,-1.0]])],"derivedFrom":subQ1}),1.0]])]});}
            var Q70;
            {var subQ0=sQuery(id+"F2.wireOp",EDGE,"E4.4");var subQ1=sQuery(id+"F2.wireOp",EDGE,"E3.5");var subQ2=makeQuery(id+"F2.imprint","INTERSECT",VERTEX,{"derivedFrom":[subQ1,subQ0]});Q70=makeQuery(id+"F2.imprint","IMPRINT",FACE,{"disambiguationData":[TD([[makeQuery(id+"F2.imprint","IMPRINT",EDGE,{"disambiguationData":[TD([[subQ2,-1.0]])],"derivedFrom":subQ1}),1.0]])]});}
            var Q71;
            {var subQ0=sQuery(id+"F2.wireOp",EDGE,"E5.1");var subQ1=sQuery(id+"F2.wireOp",EDGE,"E2.0");var subQ2=makeQuery(id+"F2.imprint","INTERSECT",VERTEX,{"derivedFrom":[subQ1,subQ0]});Q71=makeQuery(id+"F2.imprint","IMPRINT",FACE,{"disambiguationData":[TD([[makeQuery(id+"F2.imprint","IMPRINT",EDGE,{"disambiguationData":[TD([[subQ2,-1.0]])],"derivedFrom":subQ1}),1.0]])]});}
            var Q72;
            {var subQ0=sQuery(id+"F2.wireOp",EDGE,"E4.0");var subQ1=sQuery(id+"F2.wireOp",EDGE,"E3.1");var subQ2=makeQuery(id+"F2.imprint","INTERSECT",VERTEX,{"derivedFrom":[subQ1,subQ0]});Q72=makeQuery(id+"F2.imprint","IMPRINT",FACE,{"disambiguationData":[TD([[makeQuery(id+"F2.imprint","IMPRINT",EDGE,{"disambiguationData":[TD([[subQ2,-1.0]])],"derivedFrom":subQ1}),1.0]])]});}
            extrude(context, id + "F3", {"entities" : qUnion([Q0, Q1, Q2, Q3, Q4, Q5, Q6, Q7, Q8, Q9, Q10, Q11, Q12, Q13, Q14, Q15, Q16, Q17, Q18, Q19, Q20, Q21, Q22, Q23, Q24, Q25, Q26, Q27, Q28, Q29, Q30, Q31, Q32, Q33, Q34, Q35, Q36, Q37, Q38, Q39, Q40, Q41, Q42, Q43, Q44, Q45, Q46, Q47, Q48, Q49, Q50, Q51, Q52, Q53, Q54, Q55, Q56, Q57, Q58, Q59, Q60, Q61, Q62, Q63, Q64, Q65, Q66, Q67, Q68, Q69, Q70, Q71, Q72]), "operationType" : NewBodyOperationType.REMOVE, "oppositeDirection" : true, "depth" : 2.54 * mm, "offsetDistance" : 25.4 * mm});
        }
        {
            var Q0;
            Q0=makeQuery(id+"F3.boolean.opBoolean","COPY",FACE,{"derivedFrom":makeQuery(id+"F3.opExtrude","CAP_FACE",FACE,{"disambiguationData":[OSD([sQuery(id+"F2.wireOp",EDGE,"E2.0"),sQuery(id+"F2.wireOp",EDGE,"E2.1"),sQuery(id+"F2.wireOp",EDGE,"E2.2"),sQuery(id+"F2.wireOp",EDGE,"E2.3"),sQuery(id+"F2.wireOp",EDGE,"E2.4"),sQuery(id+"F2.wireOp",EDGE,"E2.5"),sQuery(id+"F2.wireOp",EDGE,"E3.0"),sQuery(id+"F2.wireOp",EDGE,"E3.1"),sQuery(id+"F2.wireOp",EDGE,"E3.2"),sQuery(id+"F2.wireOp",EDGE,"E3.3"),sQuery(id+"F2.wireOp",EDGE,"E3.4"),sQuery(id+"F2.wireOp",EDGE,"E3.5"),sQuery(id+"F2.wireOp",EDGE,"E4.0"),sQuery(id+"F2.wireOp",EDGE,"E4.1"),sQuery(id+"F2.wireOp",EDGE,"E4.2"),sQuery(id+"F2.wireOp",EDGE,"E4.3"),sQuery(id+"F2.wireOp",EDGE,"E4.4"),sQuery(id+"F2.wireOp",EDGE,"E4.5")])],"isStart":false})});
            var sketch = newSketch(context, id + "F4", { "sketchPlane" : qUnion([Q0])});
            skText(sketch, "E6", { "text": "Bell Middle School 2015-2017", "fontName": "OpenSans-Regular.ttf"});
            skText(sketch, "E7", { "text": "iSTEM", "fontName": "OpenSans-Regular.ttf"});
            const initialGuessF4  = {"E6": [-0.02618, 0.00521, 1, 0, 0.00267], "E7": [-0.00767, -0.00421, 1, 0, 0.00386]};
            skSetInitialGuess(sketch, initialGuessF4);
            skSolve(sketch);
        }
        {
            var Q0;
            Q0=qSketchRegion(id+"F4",true);
            extrude(context, id + "F5", {"entities" : qUnion([Q0]), "operationType" : NewBodyOperationType.ADD, "depth" : 1.27 * mm, "offsetDistance" : 25.4 * mm});
        }
    });
